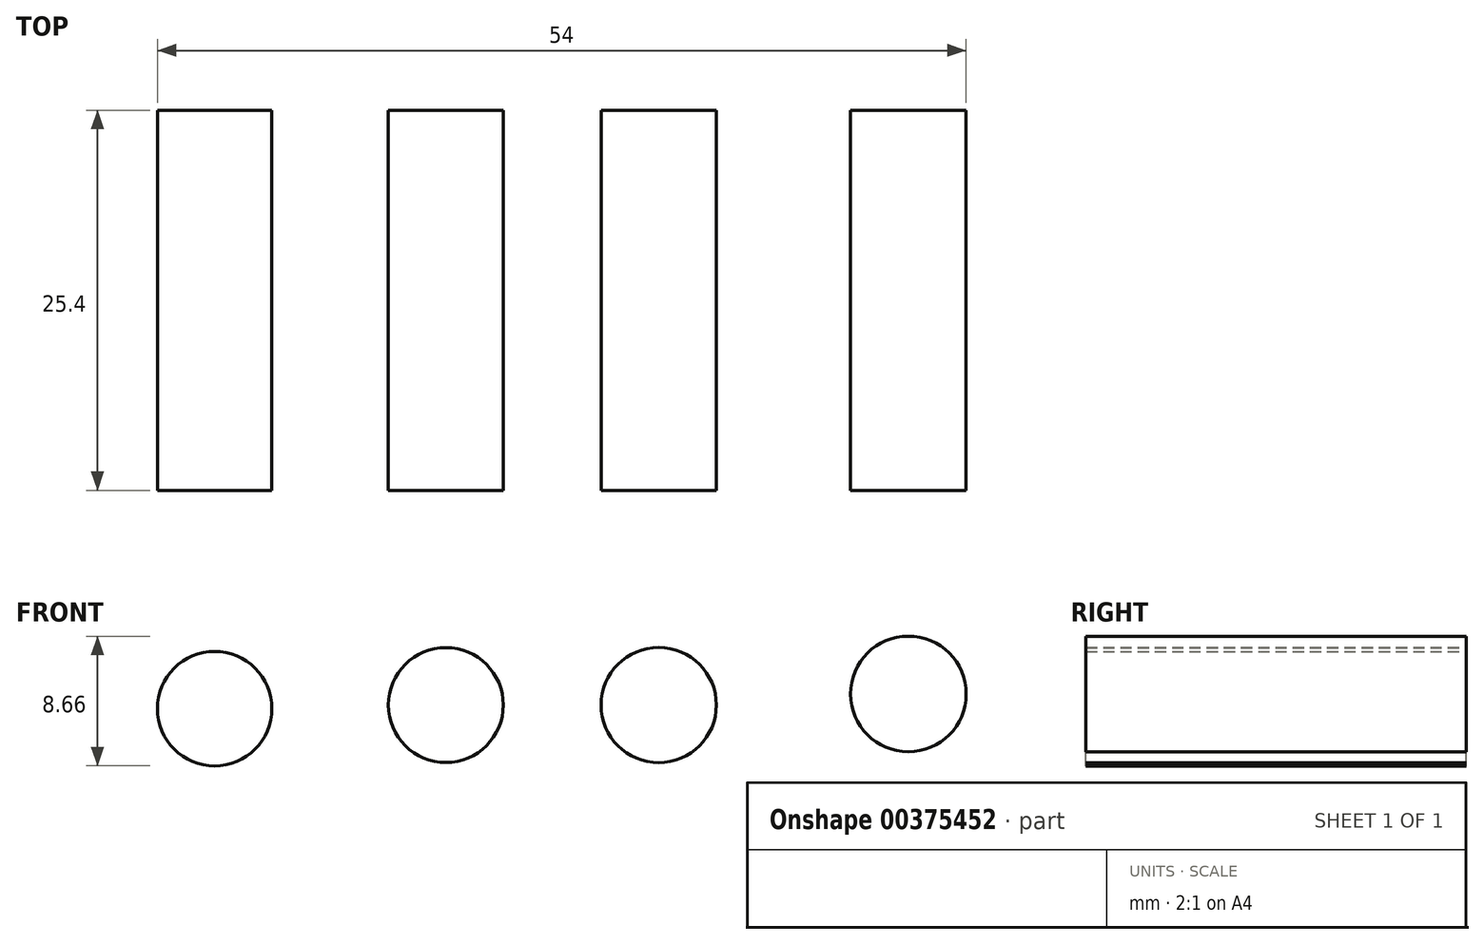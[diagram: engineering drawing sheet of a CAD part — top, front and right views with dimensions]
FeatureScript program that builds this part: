
annotation { "Feature Type Name" : "Feature", "Feature Type Description" : "" }
export const myFeature = defineFeature(function(context is Context, id is Id, definition is map)
    precondition{}
    {
        {
            var Q0;
            Q0=qCreatedBy(makeId("Front.planeOp"),FACE);
            var sketch = newSketch(context, id + "F0", { "sketchPlane" : qUnion([Q0])});
            skCircle(sketch, "E0", {"center": v(-58.08, 31) * mm, "radius": 3.82 * mm});
            skCircle(sketch, "E1", {"center": v(-42.64, 31.24) * mm, "radius": 3.84 * mm});
            skCircle(sketch, "E2", {"center": v(-28.43, 31.24) * mm, "radius": 3.85 * mm});
            skCircle(sketch, "E3", {"center": v(-11.76, 31.98) * mm, "radius": 3.86 * mm});
            skSolve(sketch);
        }
        {
            var Q0;
            Q0=makeQuery(id+"F0.imprint","IMPRINT",FACE,{"disambiguationData":[TD([[makeQuery(id+"F0.imprint","IMPRINT",EDGE,{"derivedFrom":sQuery(id+"F0.wireOp",EDGE,"ILDWCGLv-QiCo-LgLk-sLTC-FKmIEeRyNmBo.bottom")}),-1.0]])]});
            var sketch = newSketch(context, id + "F1", { "sketchPlane" : qUnion([Q0])});
            skCircle(sketch, "E4", {"center": v(-15.18, -11.37) * mm, "radius": 3.92 * mm});
            skCircle(sketch, "E5", {"center": v(9.07, 11.89) * mm, "radius": 3.89 * mm});
            skCircle(sketch, "E6", {"center": v(-15.92, 10.58) * mm, "radius": 3.91 * mm});
            skCircle(sketch, "E7", {"center": v(7.6, -10.9) * mm, "radius": 3.9 * mm});
            skSolve(sketch);
        }
        {
            var Q0;
            Q0 = qSketchRegion(id + "F1", true);
            var Q1;
            Q1 = qSketchRegion(id + "F0", true);
            extrude(context, id + "F2", {"entities" : qUnion([Q0, Q1]), "depth" : 25.4 * mm});
        }
    });
